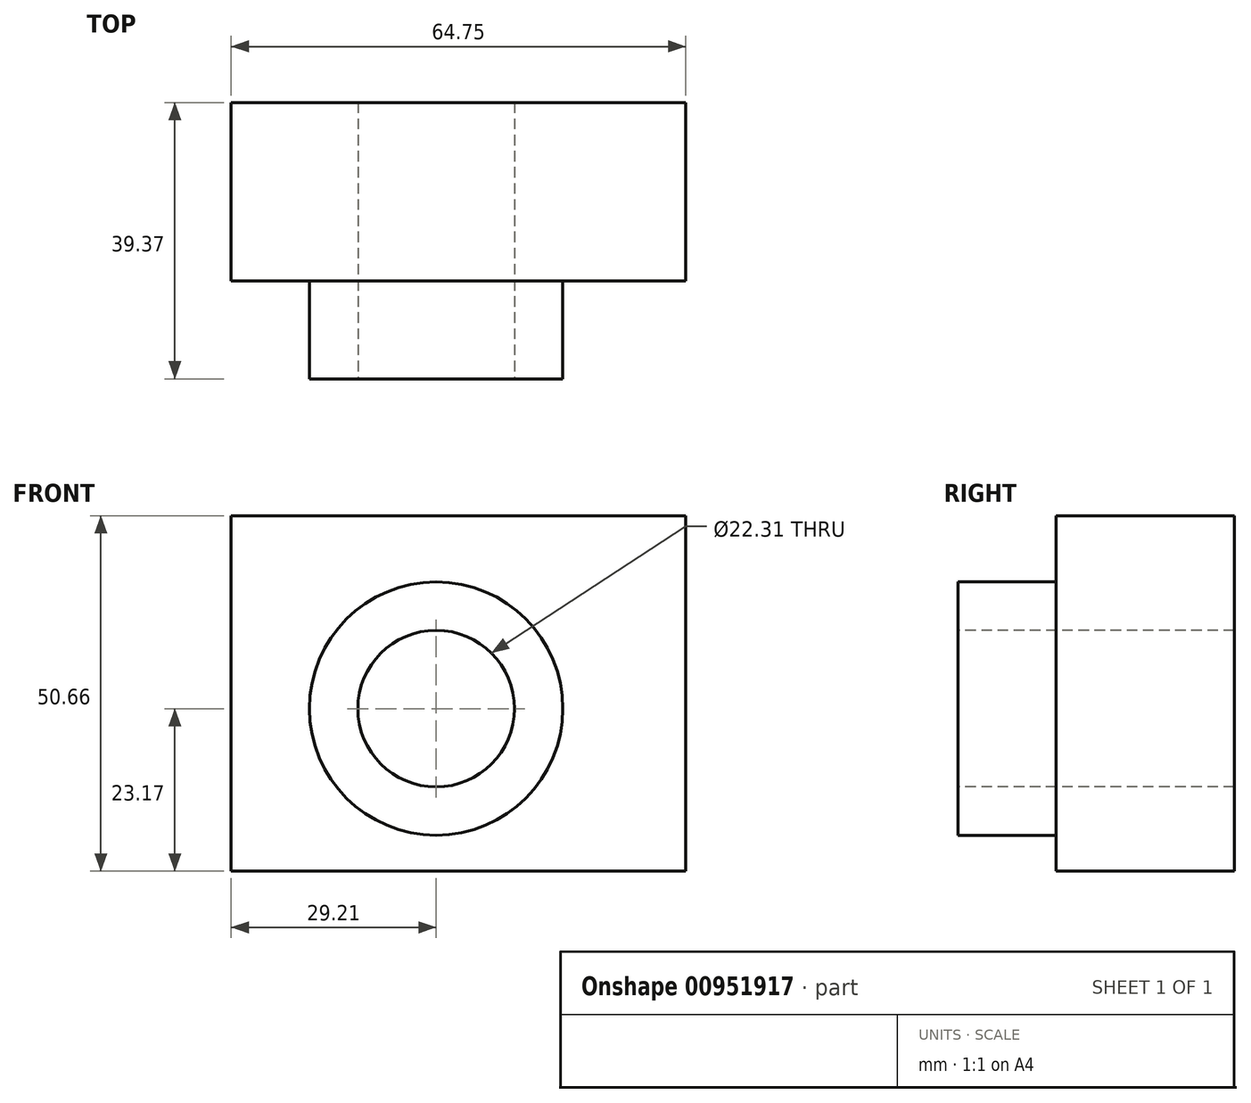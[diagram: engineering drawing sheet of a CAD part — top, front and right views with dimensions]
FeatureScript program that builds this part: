
annotation { "Feature Type Name" : "Feature", "Feature Type Description" : "" }
export const myFeature = defineFeature(function(context is Context, id is Id, definition is map)
    precondition{}
    {
        {
            var Q0;
            Q0=qCreatedBy(makeId("Front.planeOp"),FACE);
            var sketch = newSketch(context, id + "F0", { "sketchPlane" : qUnion([Q0])});
            skLineSegment(sketch, "E0.bottom", {"start": v(-29.21, 27.49) * mm, "end": v(35.54, 27.49) * mm});
            skLineSegment(sketch, "E0.top", {"start": v(-29.21, -23.17) * mm, "end": v(35.54, -23.17) * mm});
            skLineSegment(sketch, "E0.left", {"start": v(-29.21, 27.49) * mm, "end": v(-29.21, -23.17) * mm});
            skLineSegment(sketch, "E0.right", {"start": v(35.54, 27.49) * mm, "end": v(35.54, -23.17) * mm});
            skSolve(sketch);
        }
        {
            var Q0;
            Q0=makeQuery(id+"F0.imprint","IMPRINT",FACE,{"disambiguationData":[TD([[makeQuery(id+"F0.imprint","IMPRINT",EDGE,{"derivedFrom":sQuery(id+"F0.wireOp",EDGE,"E0.bottom")}),-1.0]])]});
            extrude(context, id + "F1", {"entities" : qUnion([Q0]), "depth" : 25.4 * mm, "offsetDistance" : 25.4 * mm});
        }
        {
            var Q0;
            Q0=makeQuery(id+"F1.opExtrude","CAP_FACE",FACE,{"disambiguationData":[OSD([sQuery(id+"F0.wireOp",EDGE,"E0.bottom"),sQuery(id+"F0.wireOp",EDGE,"E0.top"),sQuery(id+"F0.wireOp",EDGE,"E0.left"),sQuery(id+"F0.wireOp",EDGE,"E0.right")])],"isStart":false});
            var sketch = newSketch(context, id + "F2", { "sketchPlane" : qUnion([Q0])});
            skCircle(sketch, "E1", {"center": v(0, 0) * mm, "radius": 11.16 * mm});
            skSolve(sketch);
        }
        {
            var Q0;
            Q0=makeQuery(id+"F2.imprint","IMPRINT",FACE,{"disambiguationData":[TD([[makeQuery(id+"F2.imprint","IMPRINT",EDGE,{"derivedFrom":sQuery(id+"F2.wireOp",EDGE,"E1")}),1.0]])]});
            extrude(context, id + "F3", {"entities" : qUnion([Q0]), "operationType" : NewBodyOperationType.REMOVE, "oppositeDirection" : true, "depth" : 50.3 * mm, "offsetDistance" : 25.4 * mm});
        }
        {
            var Q0;
            Q0=makeQuery(id+"F1.opExtrude","CAP_FACE",FACE,{"disambiguationData":[OSD([sQuery(id+"F0.wireOp",EDGE,"E0.bottom"),sQuery(id+"F0.wireOp",EDGE,"E0.top"),sQuery(id+"F0.wireOp",EDGE,"E0.left"),sQuery(id+"F0.wireOp",EDGE,"E0.right")])],"isStart":false});
            var sketch = newSketch(context, id + "F4", { "sketchPlane" : qUnion([Q0])});
            skCircle(sketch, "E2", {"center": v(0, 0) * mm, "radius": 18.05 * mm});
            skSolve(sketch);
        }
        {
            var Q0;
            Q0=makeQuery(id+"F4.imprint","IMPRINT",FACE,{"disambiguationData":[TD([[makeQuery(id+"F4.imprint","IMPRINT",EDGE,{"derivedFrom":sQuery(id+"F4.wireOp",EDGE,"E2")}),1.0]])]});
            extrude(context, id + "F5", {"entities" : qUnion([Q0]), "operationType" : NewBodyOperationType.ADD, "depth" : 13.97 * mm, "offsetDistance" : 25.4 * mm});
        }
    });
